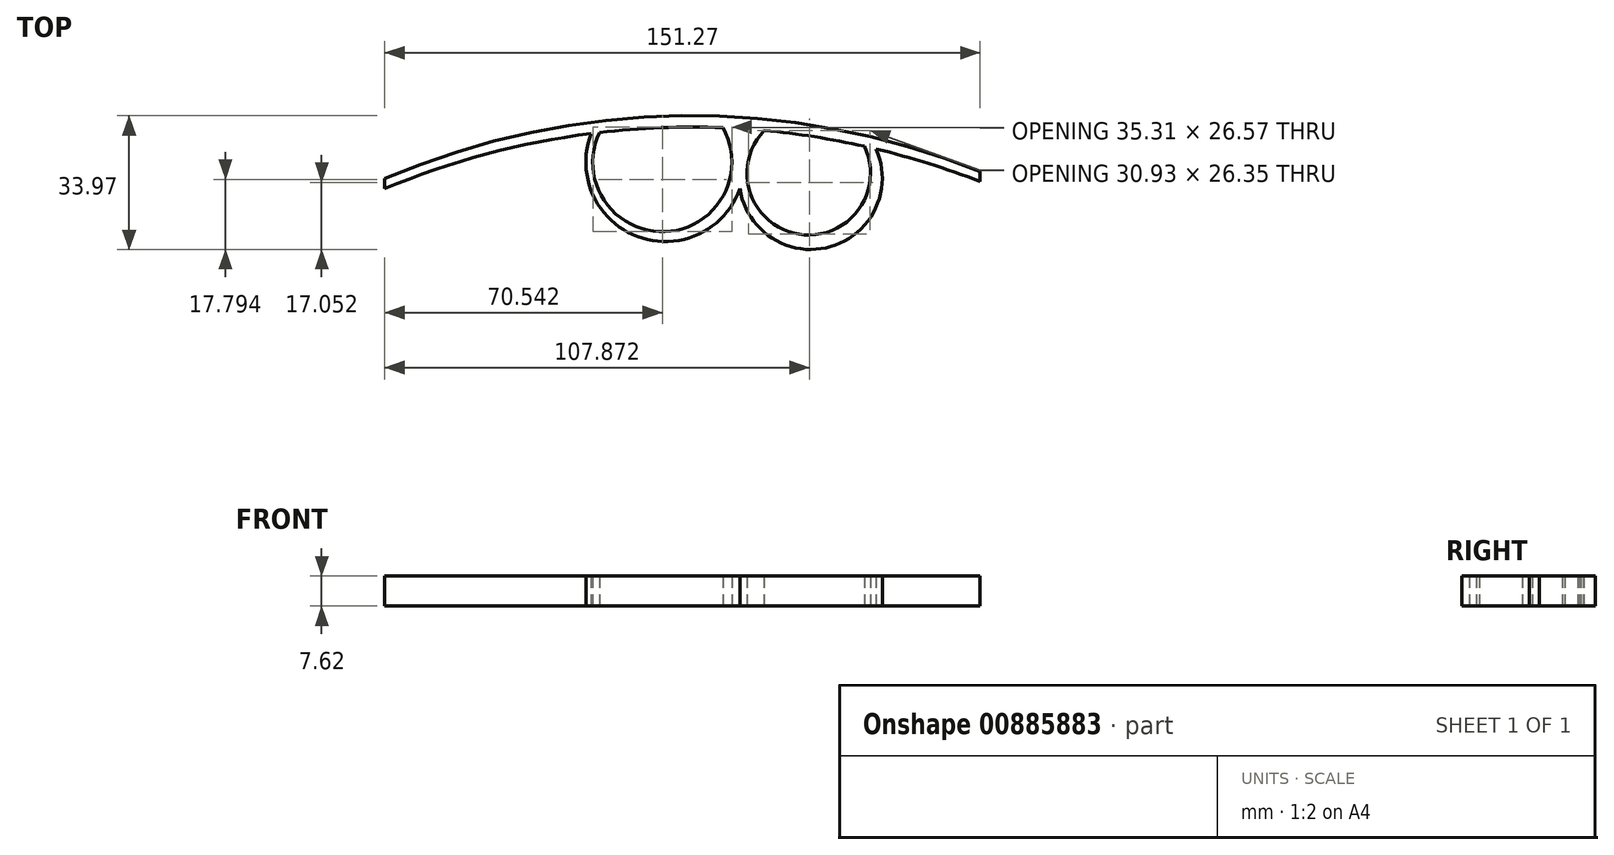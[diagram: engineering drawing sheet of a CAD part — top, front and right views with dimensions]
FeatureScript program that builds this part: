
annotation { "Feature Type Name" : "Feature", "Feature Type Description" : "" }
export const myFeature = defineFeature(function(context is Context, id is Id, definition is map)
    precondition{}
    {
        {
            var Q0;
            Q0=qCreatedBy(makeId("Top.planeOp"),FACE);
            var sketch = newSketch(context, id + "F0", { "sketchPlane" : qUnion([Q0])});
            skArc(sketch, "E0", {"start": v(54.49, -20.48) * mm, "mid": v(-21.32, -6.64) * mm, "end": v(-96.78, -22.29) * mm});
            skLineSegment(sketch, "E1", {"start": v(-96.78, -19.75) * mm, "end": v(-96.78, -22.29) * mm});
            skLineSegment(sketch, "E2", {"start": v(54.49, -17.94) * mm, "end": v(54.49, -20.48) * mm});
            skArc(sketch, "E3", {"start": v(-2.08, -7.33) * mm, "mid": v(8.54, -37.48) * mm, "end": v(28.07, -12.19) * mm});
            skArc(sketch, "E4", {"start": v(-44.32, -8.24) * mm, "mid": v(-32.57, -34.44) * mm, "end": v(-6.55, -22.29) * mm});
            skArc(sketch, "E5", {"start": v(54.49, -17.94) * mm, "mid": v(-21.33, -3.75) * mm, "end": v(-96.78, -19.75) * mm});
            skArc(sketch, "E6", {"start": v(-42.24, -7.99) * mm, "mid": v(-25.59, -33.2) * mm, "end": v(-10.9, -6.79) * mm});
            skArc(sketch, "E7", {"start": v(-0.4, -7.48) * mm, "mid": v(8.5, -33.83) * mm, "end": v(25.05, -11.49) * mm});
            skLineSegment(sketch, "E8", {"start": v(-94.17, -18.65) * mm, "end": v(-94.17, -15.64) * mm});
            skLineSegment(sketch, "E9", {"start": v(-94.17, -15.64) * mm, "end": v(-91.14, -17.43) * mm});
            skLineSegment(sketch, "E10", {"start": v(-91.14, -17.43) * mm, "end": v(-91.14, -13.15) * mm});
            skLineSegment(sketch, "E11", {"start": v(-91.14, -13.15) * mm, "end": v(-88.64, -16.46) * mm});
            skLineSegment(sketch, "E12", {"start": v(-88.64, -16.46) * mm, "end": v(-88.64, -9.9) * mm});
            skLineSegment(sketch, "E13", {"start": v(-88.64, -9.9) * mm, "end": v(-83.67, -14.66) * mm});
            skLineSegment(sketch, "E14", {"start": v(-83.67, -14.66) * mm, "end": v(-83.67, -7.91) * mm});
            skLineSegment(sketch, "E15", {"start": v(-83.67, -7.91) * mm, "end": v(-79.14, -13.15) * mm});
            skLineSegment(sketch, "E16", {"start": v(-79.14, -13.15) * mm, "end": v(-77.08, -5.17) * mm});
            skLineSegment(sketch, "E17", {"start": v(-77.08, -5.17) * mm, "end": v(-73.34, -9.9) * mm});
            skLineSegment(sketch, "E18", {"start": v(-73.34, -9.9) * mm, "end": v(-73.34, -5.17) * mm});
            skLineSegment(sketch, "E19", {"start": v(-73.34, -5.17) * mm, "end": v(-67.9, -9.9) * mm});
            skLineSegment(sketch, "E20", {"start": v(-67.9, -9.9) * mm, "end": v(-67.9, -2.93) * mm});
            skLineSegment(sketch, "E21", {"start": v(-67.9, -2.93) * mm, "end": v(-63.62, -5.17) * mm});
            skLineSegment(sketch, "E22", {"start": v(-63.62, -5.17) * mm, "end": v(-58.38, 0) * mm});
            skLineSegment(sketch, "E23", {"start": v(-58.38, 0) * mm, "end": v(-58.38, -7.72) * mm});
            skLineSegment(sketch, "E24", {"start": v(-58.38, -7.72) * mm, "end": v(-51.65, 0) * mm});
            skLineSegment(sketch, "E25", {"start": v(-51.65, 0) * mm, "end": v(-45.72, -5.17) * mm});
            skLineSegment(sketch, "E26", {"start": v(-45.72, -5.17) * mm, "end": v(-37.36, -2.5) * mm});
            skLineSegment(sketch, "E27", {"start": v(-37.36, -2.5) * mm, "end": v(-34.11, -2.93) * mm});
            skLineSegment(sketch, "E28", {"start": v(-34.11, -2.93) * mm, "end": v(-30.96, 3.55) * mm});
            skLineSegment(sketch, "E29", {"start": v(-30.96, 3.55) * mm, "end": v(-27.96, -3.94) * mm});
            skLineSegment(sketch, "E30", {"start": v(-27.96, -3.94) * mm, "end": v(-22.49, 3.55) * mm});
            skLineSegment(sketch, "E31", {"start": v(-22.49, 3.55) * mm, "end": v(-21.33, -3.75) * mm});
            skLineSegment(sketch, "E32", {"start": v(-21.33, -3.75) * mm, "end": v(-16.76, 3.55) * mm});
            skLineSegment(sketch, "E33", {"start": v(-16.76, 3.55) * mm, "end": v(-14, -3.8) * mm});
            skLineSegment(sketch, "E34", {"start": v(-14, -3.8) * mm, "end": v(-8.78, 3.55) * mm});
            skLineSegment(sketch, "E35", {"start": v(-8.78, 3.55) * mm, "end": v(-6.82, -4.11) * mm});
            skLineSegment(sketch, "E36", {"start": v(-6.82, -4.11) * mm, "end": v(-2.3, 3.55) * mm});
            skLineSegment(sketch, "E37", {"start": v(-2.3, 3.55) * mm, "end": v(0, -4.65) * mm});
            skLineSegment(sketch, "E38", {"start": v(0, -4.65) * mm, "end": v(3.18, 3.55) * mm});
            skLineSegment(sketch, "E39", {"start": v(3.18, 3.55) * mm, "end": v(4.77, -5.17) * mm});
            skLineSegment(sketch, "E40", {"start": v(4.77, -5.17) * mm, "end": v(9.17, 3.55) * mm});
            skLineSegment(sketch, "E41", {"start": v(9.17, 3.55) * mm, "end": v(12.8, -6.31) * mm});
            skLineSegment(sketch, "E42", {"start": v(12.8, -6.31) * mm, "end": v(16.9, 3.55) * mm});
            skLineSegment(sketch, "E43", {"start": v(16.9, 3.55) * mm, "end": v(20.45, -7.72) * mm});
            skLineSegment(sketch, "E44", {"start": v(20.45, -7.72) * mm, "end": v(23.62, 3.55) * mm});
            skLineSegment(sketch, "E45", {"start": v(23.62, 3.55) * mm, "end": v(27.45, -9.28) * mm});
            skLineSegment(sketch, "E46", {"start": v(27.45, -9.28) * mm, "end": v(30.85, 3.55) * mm});
            skLineSegment(sketch, "E47", {"start": v(30.85, 3.55) * mm, "end": v(36, -11.55) * mm});
            skLineSegment(sketch, "E48", {"start": v(36, -11.55) * mm, "end": v(38.08, 3.55) * mm});
            skLineSegment(sketch, "E49", {"start": v(38.08, 3.55) * mm, "end": v(41.2, -13.15) * mm});
            skLineSegment(sketch, "E50", {"start": v(41.2, -13.15) * mm, "end": v(44.06, 3.55) * mm});
            skLineSegment(sketch, "E51", {"start": v(44.06, 3.55) * mm, "end": v(48.49, -15.64) * mm});
            skLineSegment(sketch, "E52", {"start": v(48.49, -15.64) * mm, "end": v(51.04, 3.55) * mm});
            skLineSegment(sketch, "E53", {"start": v(51.04, 3.55) * mm, "end": v(54.49, -17.94) * mm});
            skSolve(sketch);
        }
        {
            var Q0;
            {var subQ1=sQuery(id+"F0.wireOp",EDGE,"E1");Q0=makeQuery(id+"F0.imprint","IMPRINT",FACE,{"disambiguationData":[TD([[makeQuery(id+"F0.imprint","IMPRINT",EDGE,{"derivedFrom":subQ1}),1.0]])]});}
            var Q1;
            {var subQ0=sQuery(id+"F0.wireOp",EDGE,"E4");Q1=makeQuery(id+"F0.imprint","IMPRINT",FACE,{"disambiguationData":[TD([[makeQuery(id+"F0.imprint","IMPRINT",EDGE,{"derivedFrom":subQ0}),1.0]])]});}
            var Q2;
            {var subQ4=sQuery(id+"F0.wireOp",EDGE,"E7");Q2=makeQuery(id+"F0.imprint","IMPRINT",FACE,{"disambiguationData":[TD([[makeQuery(id+"F0.imprint","IMPRINT",EDGE,{"derivedFrom":subQ4}),-1.0]])]});}
            var Q3;
            {var subQ0=sQuery(id+"F0.wireOp",EDGE,"jZFIun4f-p3tJ-XqvO-niAz-WnIYnR2MKS4q");Q3=makeQuery(id+"F0.imprint","IMPRINT",FACE,{"disambiguationData":[TD([[makeQuery(id+"F0.imprint","IMPRINT",EDGE,{"derivedFrom":subQ0}),-1.0]])]});}
            var Q4;
            {var subQ0=sQuery(id+"F0.wireOp",EDGE,"CpPpHHJt-TjSS-xgC1-iXG4-c97LWkXSSzzi");Q4=makeQuery(id+"F0.imprint","IMPRINT",FACE,{"disambiguationData":[TD([[makeQuery(id+"F0.imprint","IMPRINT",EDGE,{"derivedFrom":subQ0}),-1.0]])]});}
            var Q5;
            {var subQ0=sQuery(id+"F0.wireOp",EDGE,"LUNSHice-m1qO-c4p8-uycQ-QW7PsIfn1O6y");Q5=makeQuery(id+"F0.imprint","IMPRINT",FACE,{"disambiguationData":[TD([[makeQuery(id+"F0.imprint","IMPRINT",EDGE,{"derivedFrom":subQ0}),-1.0]])]});}
            extrude(context, id + "F1", {"entities" : qUnion([Q0, Q1, Q2, Q3, Q4, Q5]), "depth" : 7.62 * mm, "offsetDistance" : 25.4 * mm});
        }
    });
